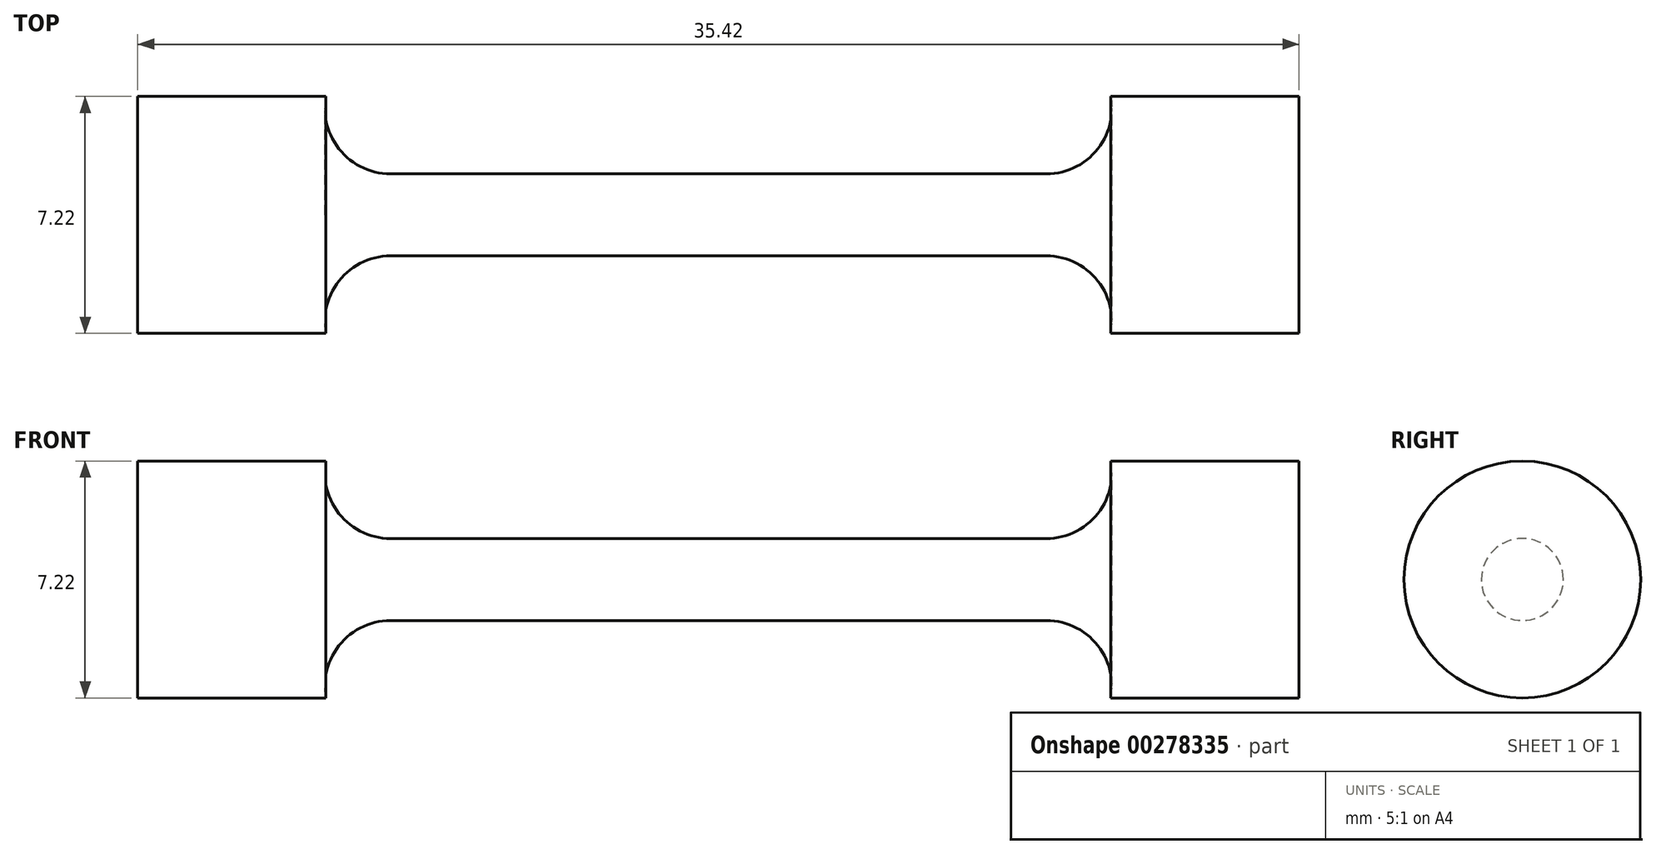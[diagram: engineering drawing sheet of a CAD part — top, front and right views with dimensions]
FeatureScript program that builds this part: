
annotation { "Feature Type Name" : "Feature", "Feature Type Description" : "" }
export const myFeature = defineFeature(function(context is Context, id is Id, definition is map)
    precondition{}
    {
        {
            var Q0;
            Q0=qCreatedBy(makeId("Front.planeOp"),FACE);
            var sketch = newSketch(context, id + "F0", { "sketchPlane" : qUnion([Q0])});
            skLineSegment(sketch, "E0", {"start": v(0, 1.25) * mm, "end": v(10, 1.25) * mm});
            skArc(sketch, "E1", {"start": v(10, 1.25) * mm, "mid": v(11.54, 1.97) * mm, "end": v(11.97, 3.61) * mm});
            skLineSegment(sketch, "E2", {"start": v(11.97, 3.61) * mm, "end": v(17.71, 3.61) * mm});
            skLineSegment(sketch, "E3", {"start": v(17.71, 3.61) * mm, "end": v(17.71, 0) * mm});
            skLineSegment(sketch, "E4.MirrorCS", {"start": v(0, 1.25) * mm, "end": v(-10, 1.25) * mm});
            skLineSegment(sketch, "E5.MirrorCS", {"start": v(-17.71, 3.61) * mm, "end": v(-17.71, 0) * mm});
            skLineSegment(sketch, "E6.MirrorCS", {"start": v(-11.97, 3.61) * mm, "end": v(-17.71, 3.61) * mm});
            skArc(sketch, "E7.MirrorCS", {"start": v(-10, 1.25) * mm, "mid": v(-11.54, 1.97) * mm, "end": v(-11.97, 3.61) * mm});
            skLineSegment(sketch, "E8", {"start": v(-17.71, 0) * mm, "end": v(17.71, 0) * mm});
            skSolve(sketch);
        }
        {
            var Q0;
            Q0 = qSketchRegion(id + "F0", true);
            var Q1;
            Q1=sQuery(id+"F0.wireOp",EDGE,"E8");
            revolve(context, id + "F1", {"entities" : qUnion([Q0]), "axis" : qUnion([Q1]), "revolveType" : RevolveType.FULL});
        }
    });
